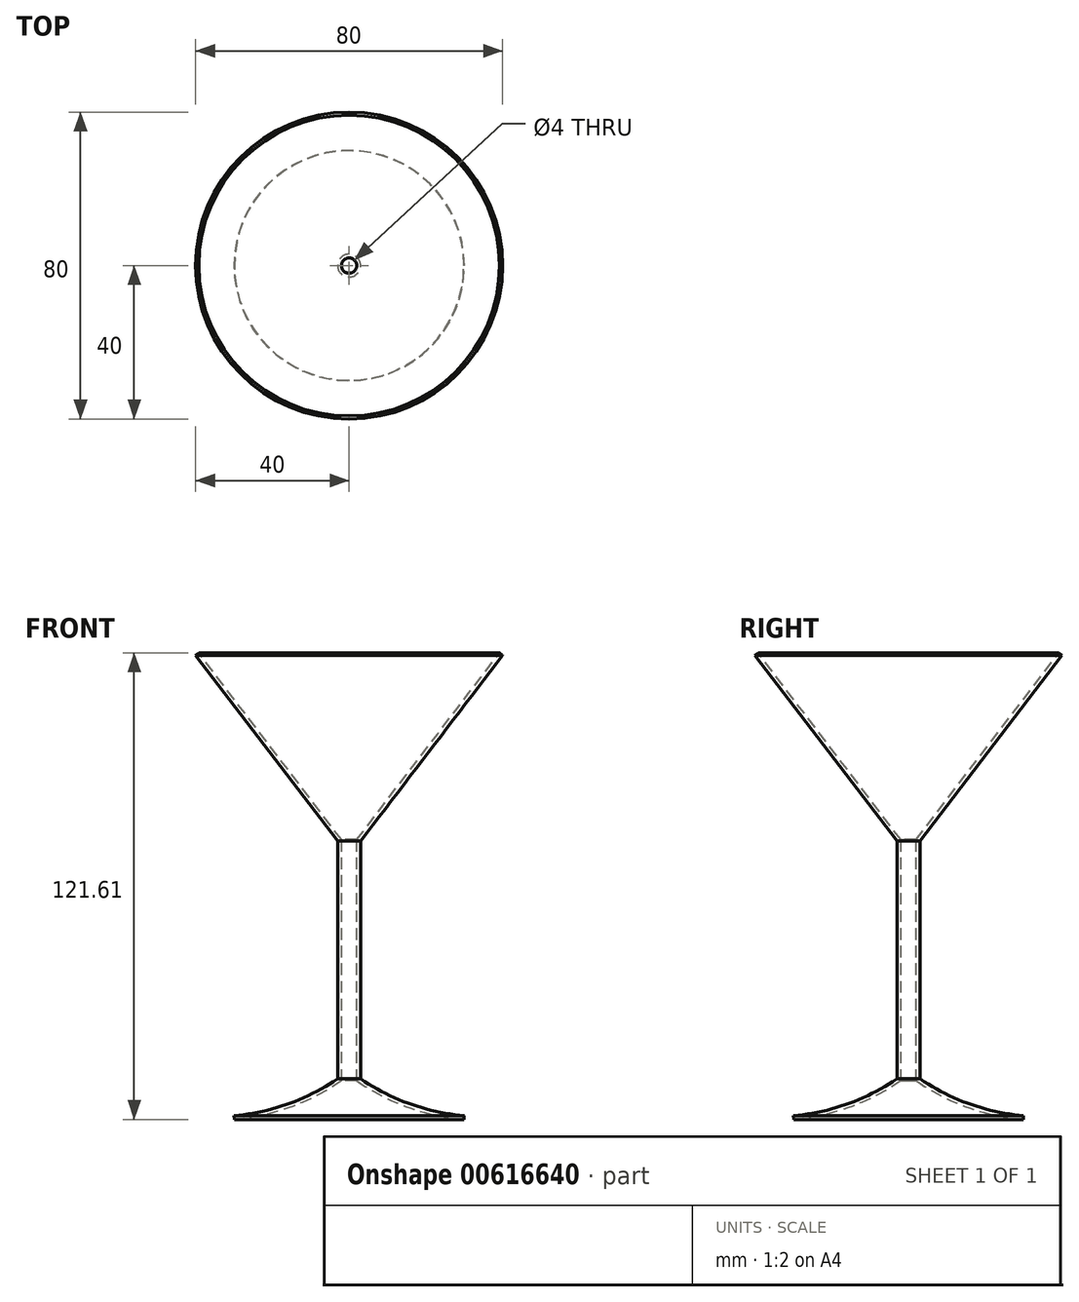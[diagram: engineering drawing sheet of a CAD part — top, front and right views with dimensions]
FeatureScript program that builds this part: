
annotation { "Feature Type Name" : "Feature", "Feature Type Description" : "" }
export const myFeature = defineFeature(function(context is Context, id is Id, definition is map)
    precondition{}
    {
        {
            var Q0;
            Q0=qCreatedBy(makeId("Front.planeOp"),FACE);
            var sketch = newSketch(context, id + "F0", { "sketchPlane" : qUnion([Q0])});
            skLineSegment(sketch, "E0", {"start": v(-40, 93.15) * mm, "end": v(-3, 44.75) * mm});
            skLineSegment(sketch, "E1", {"start": v(-3, 44.75) * mm, "end": v(-3, -17.27) * mm});
            skArc(sketch, "E2", {"start": v(-30, -26.85) * mm, "mid": v(-15.88, -23.8) * mm, "end": v(-3, -17.27) * mm});
            skLineSegment(sketch, "E3", {"start": v(0, 101.97) * mm, "end": v(0, -35.92) * mm, "construction": true});
            skArc(sketch, "E4.0", {"start": v(-29.92, -27.85) * mm, "mid": v(-15.3, -24.66) * mm, "end": v(-2, -17.8) * mm});
            skLineSegment(sketch, "E4.1", {"start": v(-2, 45.09) * mm, "end": v(-2, -17.8) * mm});
            skLineSegment(sketch, "E4.2", {"start": v(-39.2, 93.76) * mm, "end": v(-2, 45.09) * mm});
            skLineSegment(sketch, "E5", {"start": v(-39.2, 93.76) * mm, "end": v(-40, 93.15) * mm});
            skLineSegment(sketch, "E6", {"start": v(-29.92, -27.85) * mm, "end": v(-30, -26.85) * mm});
            skSolve(sketch);
        }
        {
            var Q0;
            Q0=makeQuery(id+"F0.imprint","IMPRINT",FACE,{"disambiguationData":[TD([[makeQuery(id+"F0.imprint","IMPRINT",EDGE,{"derivedFrom":sQuery(id+"F0.wireOp",EDGE,"E0")}),1.0]])]});
            var Q1;
            Q1=sQuery(id+"F0.wireOp",EDGE,"E3");
            revolve(context, id + "F1", {"entities" : qUnion([Q0]), "axis" : qUnion([Q1]), "revolveType" : RevolveType.FULL});
        }
    });
